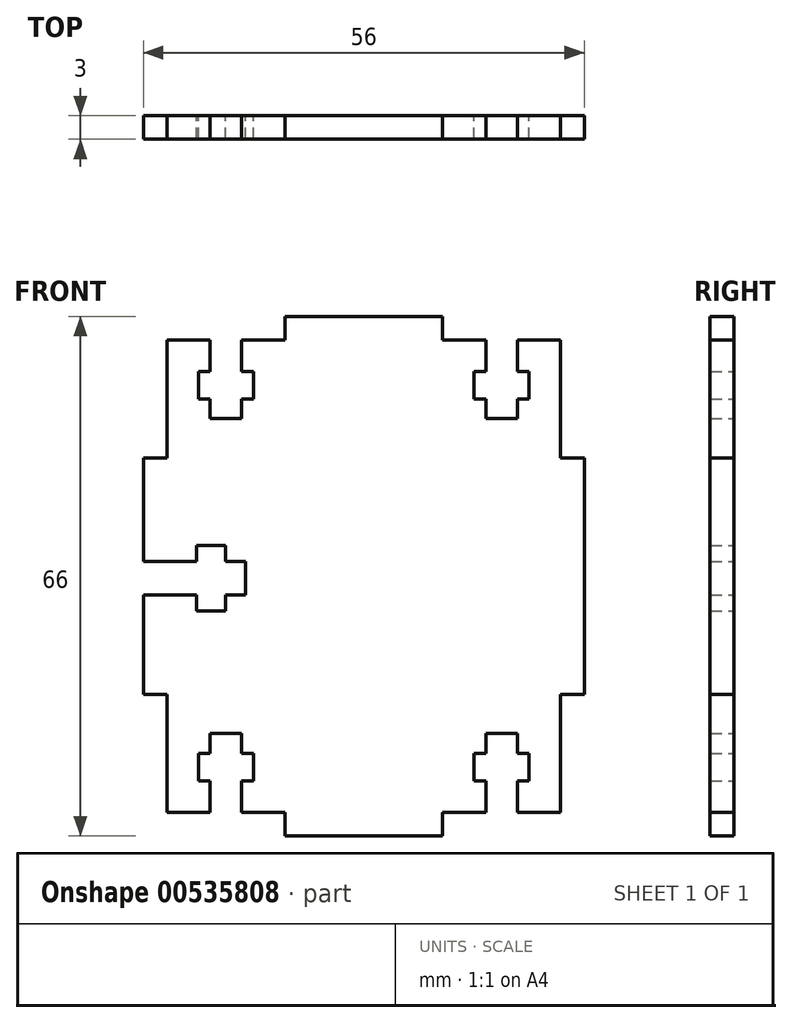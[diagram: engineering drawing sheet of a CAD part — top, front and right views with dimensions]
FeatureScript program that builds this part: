
annotation { "Feature Type Name" : "Feature", "Feature Type Description" : "" }
export const myFeature = defineFeature(function(context is Context, id is Id, definition is map)
    precondition{}
    {
        {
            var Q0;
            Q0=qCreatedBy(makeId("Front.planeOp"),FACE);
            var sketch = newSketch(context, id + "F0", { "sketchPlane" : qUnion([Q0])});
            skLineSegment(sketch, "E0.bottom", {"start": v(-25, 30) * mm, "end": v(-19.5, 30) * mm});
            skPoint(sketch, "E0.middle", {"position": v(0, 0) * mm});
            skLineSegment(sketch, "E1.bottom", {"start": v(-10, 33) * mm, "end": v(10, 33) * mm});
            skLineSegment(sketch, "E1.left", {"start": v(-10, 33) * mm, "end": v(-10, 30) * mm});
            skLineSegment(sketch, "E1.right", {"start": v(10, 33) * mm, "end": v(10, 30) * mm});
            skLineSegment(sketch, "E2.trimOffspring", {"start": v(10, 30) * mm, "end": v(15.5, 30) * mm});
            skLineSegment(sketch, "E3.left", {"start": v(-19.5, 30) * mm, "end": v(-19.5, 26) * mm});
            skLineSegment(sketch, "E4.bottom", {"start": v(-21, 26) * mm, "end": v(-19.5, 26) * mm});
            skLineSegment(sketch, "E4.top", {"start": v(-21, 22.5) * mm, "end": v(-19.5, 22.5) * mm});
            skLineSegment(sketch, "E4.left", {"start": v(-21, 26) * mm, "end": v(-21, 22.5) * mm});
            skLineSegment(sketch, "E5", {"start": v(-17.5, 30) * mm, "end": v(-17.5, 11.76) * mm, "construction": true});
            skLineSegment(sketch, "E6.trimOffspring", {"start": v(-19.5, 22.5) * mm, "end": v(-19.5, 20) * mm});
            skLineSegment(sketch, "E7.MirrorCS", {"start": v(-15.5, 22.5) * mm, "end": v(-15.5, 20) * mm});
            skLineSegment(sketch, "E8.MirrorCS", {"start": v(-14, 26) * mm, "end": v(-14, 22.5) * mm});
            skLineSegment(sketch, "E9.MirrorCS", {"start": v(-14, 26) * mm, "end": v(-15.5, 26) * mm});
            skLineSegment(sketch, "E10.MirrorCS", {"start": v(-15.5, 30) * mm, "end": v(-15.5, 26) * mm});
            skLineSegment(sketch, "E11.MirrorCS", {"start": v(-14, 22.5) * mm, "end": v(-15.5, 22.5) * mm});
            skLineSegment(sketch, "E12", {"start": v(-19.5, 20) * mm, "end": v(-15.5, 20) * mm});
            skPoint(sketch, "E3.bottom.end.orphan", {"position": v(-15.5, 30) * mm});
            skLineSegment(sketch, "E13.trimOffspring", {"start": v(-15.5, 30) * mm, "end": v(-10, 30) * mm});
            skLineSegment(sketch, "E14.MirrorCS", {"start": v(14, 26) * mm, "end": v(15.5, 26) * mm});
            skLineSegment(sketch, "E15.MirrorCS", {"start": v(14, 26) * mm, "end": v(14, 22.5) * mm});
            skLineSegment(sketch, "E16.MirrorCS", {"start": v(19.5, 30) * mm, "end": v(19.5, 26) * mm});
            skLineSegment(sketch, "E17.MirrorCS", {"start": v(14, 22.5) * mm, "end": v(15.5, 22.5) * mm});
            skPoint(sketch, "E18.MirrorP", {"position": v(15.5, 30) * mm});
            skLineSegment(sketch, "E19.MirrorCS", {"start": v(21, 22.5) * mm, "end": v(19.5, 22.5) * mm});
            skLineSegment(sketch, "E20.MirrorCS", {"start": v(15.5, 22.5) * mm, "end": v(15.5, 20) * mm});
            skLineSegment(sketch, "E21.MirrorCS", {"start": v(19.5, 22.5) * mm, "end": v(19.5, 20) * mm});
            skLineSegment(sketch, "E22.MirrorCS", {"start": v(21, 26) * mm, "end": v(21, 22.5) * mm});
            skLineSegment(sketch, "E23.MirrorCS", {"start": v(19.5, 20) * mm, "end": v(15.5, 20) * mm});
            skLineSegment(sketch, "E24.MirrorCS", {"start": v(15.5, 30) * mm, "end": v(15.5, 26) * mm});
            skLineSegment(sketch, "E25.MirrorCS", {"start": v(21, 26) * mm, "end": v(19.5, 26) * mm});
            skLineSegment(sketch, "E26.MirrorCS", {"start": v(-10, -33) * mm, "end": v(-10, -30) * mm});
            skLineSegment(sketch, "E27.MirrorCS", {"start": v(10, -33) * mm, "end": v(10, -30) * mm});
            skLineSegment(sketch, "E28.MirrorCS", {"start": v(-19.5, -30) * mm, "end": v(-19.5, -26) * mm});
            skLineSegment(sketch, "E29.MirrorCS", {"start": v(19.5, -20) * mm, "end": v(15.5, -20) * mm});
            skLineSegment(sketch, "E30.MirrorCS", {"start": v(-21, -26) * mm, "end": v(-19.5, -26) * mm});
            skLineSegment(sketch, "E31.MirrorCS", {"start": v(14, -26) * mm, "end": v(15.5, -26) * mm});
            skLineSegment(sketch, "E32.MirrorCS", {"start": v(14, -26) * mm, "end": v(14, -22.5) * mm});
            skLineSegment(sketch, "E33.MirrorCS", {"start": v(-21, -22.5) * mm, "end": v(-19.5, -22.5) * mm});
            skLineSegment(sketch, "E34.MirrorCS", {"start": v(-21, -26) * mm, "end": v(-21, -22.5) * mm});
            skLineSegment(sketch, "E35.MirrorCS", {"start": v(-14, -26) * mm, "end": v(-15.5, -26) * mm});
            skLineSegment(sketch, "E36.MirrorCS", {"start": v(14, -22.5) * mm, "end": v(15.5, -22.5) * mm});
            skLineSegment(sketch, "E37.MirrorCS", {"start": v(15.5, -30) * mm, "end": v(15.5, -26) * mm});
            skLineSegment(sketch, "E38.MirrorCS", {"start": v(21, -26) * mm, "end": v(19.5, -26) * mm});
            skLineSegment(sketch, "E39.MirrorCS", {"start": v(-15.5, -30) * mm, "end": v(-15.5, -26) * mm});
            skLineSegment(sketch, "E40.MirrorCS", {"start": v(-14, -26) * mm, "end": v(-14, -22.5) * mm});
            skLineSegment(sketch, "E41.MirrorCS", {"start": v(-19.5, -20) * mm, "end": v(-15.5, -20) * mm});
            skLineSegment(sketch, "E42.MirrorCS", {"start": v(21, -26) * mm, "end": v(21, -22.5) * mm});
            skLineSegment(sketch, "E43.MirrorCS", {"start": v(21, -22.5) * mm, "end": v(19.5, -22.5) * mm});
            skLineSegment(sketch, "E44.MirrorCS", {"start": v(-14, -22.5) * mm, "end": v(-15.5, -22.5) * mm});
            skLineSegment(sketch, "E45.MirrorCS", {"start": v(10, -30) * mm, "end": v(15.5, -30) * mm});
            skLineSegment(sketch, "E46.MirrorCS", {"start": v(-15.5, -30) * mm, "end": v(-10, -30) * mm});
            skLineSegment(sketch, "E47.MirrorCS", {"start": v(19.5, -30) * mm, "end": v(19.5, -26) * mm});
            skLineSegment(sketch, "E48.MirrorCS", {"start": v(-25, -30) * mm, "end": v(-19.5, -30) * mm});
            skPoint(sketch, "E49.MirrorP", {"position": v(-15.5, -30) * mm});
            skLineSegment(sketch, "E50.MirrorCS", {"start": v(-10, -33) * mm, "end": v(10, -33) * mm});
            skPoint(sketch, "E51.MirrorP", {"position": v(15.5, -30) * mm});
            skLineSegment(sketch, "E52.MirrorCS", {"start": v(-17.5, -30) * mm, "end": v(-17.5, -11.76) * mm, "construction": true});
            skLineSegment(sketch, "E53.MirrorCS", {"start": v(-19.5, -22.5) * mm, "end": v(-19.5, -20) * mm});
            skLineSegment(sketch, "E54.MirrorCS", {"start": v(-15.5, -22.5) * mm, "end": v(-15.5, -20) * mm});
            skLineSegment(sketch, "E55.MirrorCS", {"start": v(19.5, -22.5) * mm, "end": v(19.5, -20) * mm});
            skLineSegment(sketch, "E56.MirrorCS", {"start": v(15.5, -22.5) * mm, "end": v(15.5, -20) * mm});
            skLineSegment(sketch, "E57", {"start": v(-25, 30) * mm, "end": v(-25, 15) * mm});
            skLineSegment(sketch, "E58", {"start": v(25, 30) * mm, "end": v(25, 15) * mm});
            skLineSegment(sketch, "E59.trimOffspring", {"start": v(19.5, 30) * mm, "end": v(25, 30) * mm});
            skLineSegment(sketch, "E60.trimOffspring", {"start": v(19.5, -30) * mm, "end": v(25, -30) * mm});
            skLineSegment(sketch, "E61", {"start": v(17.5, 20) * mm, "end": v(17.5, 30) * mm, "construction": true});
            skLineSegment(sketch, "E62.bottom", {"start": v(-28, 15) * mm, "end": v(-25, 15) * mm});
            skLineSegment(sketch, "E62.top", {"start": v(-28, -15) * mm, "end": v(-25, -15) * mm});
            skLineSegment(sketch, "E62.left", {"start": v(-28, 15) * mm, "end": v(-28, -15) * mm});
            skLineSegment(sketch, "E63.trimOffspring", {"start": v(-25, -15) * mm, "end": v(-25, -30) * mm});
            skLineSegment(sketch, "E64.MirrorCS", {"start": v(28, -15) * mm, "end": v(25, -15) * mm});
            skLineSegment(sketch, "E65.MirrorCS", {"start": v(28, 15) * mm, "end": v(25, 15) * mm});
            skLineSegment(sketch, "E66.MirrorCS", {"start": v(28, 15) * mm, "end": v(28, -15) * mm});
            skLineSegment(sketch, "E67.trimOffspring", {"start": v(25, -15) * mm, "end": v(25, -30) * mm});
            skLineSegment(sketch, "E68.bottom", {"start": v(-28, 1.86) * mm, "end": v(-21.23, 1.86) * mm});
            skLineSegment(sketch, "E68.top", {"start": v(-28, -2.36) * mm, "end": v(-21.23, -2.36) * mm});
            skLineSegment(sketch, "E68.left", {"start": v(-28, 1.86) * mm, "end": v(-28, -2.36) * mm});
            skLineSegment(sketch, "E68.right", {"start": v(-15.03, 1.86) * mm, "end": v(-15.03, -2.36) * mm});
            skLineSegment(sketch, "E69.bottom", {"start": v(-21.23, 3.88) * mm, "end": v(-17.59, 3.88) * mm});
            skLineSegment(sketch, "E69.top", {"start": v(-21.23, -4.41) * mm, "end": v(-17.59, -4.41) * mm});
            skLineSegment(sketch, "E69.left", {"start": v(-21.23, 3.88) * mm, "end": v(-21.23, 1.86) * mm});
            skLineSegment(sketch, "E69.right", {"start": v(-17.59, 3.88) * mm, "end": v(-17.59, 1.86) * mm});
            skLineSegment(sketch, "E70.trimOffspring", {"start": v(-17.59, 1.86) * mm, "end": v(-15.03, 1.86) * mm});
            skLineSegment(sketch, "E71.trimOffspring", {"start": v(-21.23, -2.36) * mm, "end": v(-21.23, -4.41) * mm});
            skLineSegment(sketch, "E72.trimOffspring", {"start": v(-17.59, -2.36) * mm, "end": v(-17.59, -4.41) * mm});
            skLineSegment(sketch, "E73.trimOffspring", {"start": v(-17.59, -2.36) * mm, "end": v(-15.03, -2.36) * mm});
            skSolve(sketch);
        }
        {
            var Q0;
            Q0=makeQuery(id+"F0.imprint","IMPRINT",FACE,{"disambiguationData":[TD([[makeQuery(id+"F0.imprint","IMPRINT",EDGE,{"derivedFrom":sQuery(id+"F0.wireOp",EDGE,"E0.bottom")}),-1.0]])]});
            extrude(context, id + "F1", {"entities" : qUnion([Q0]), "depth" : 3 * mm, "offsetDistance" : 25 * mm});
        }
    });
